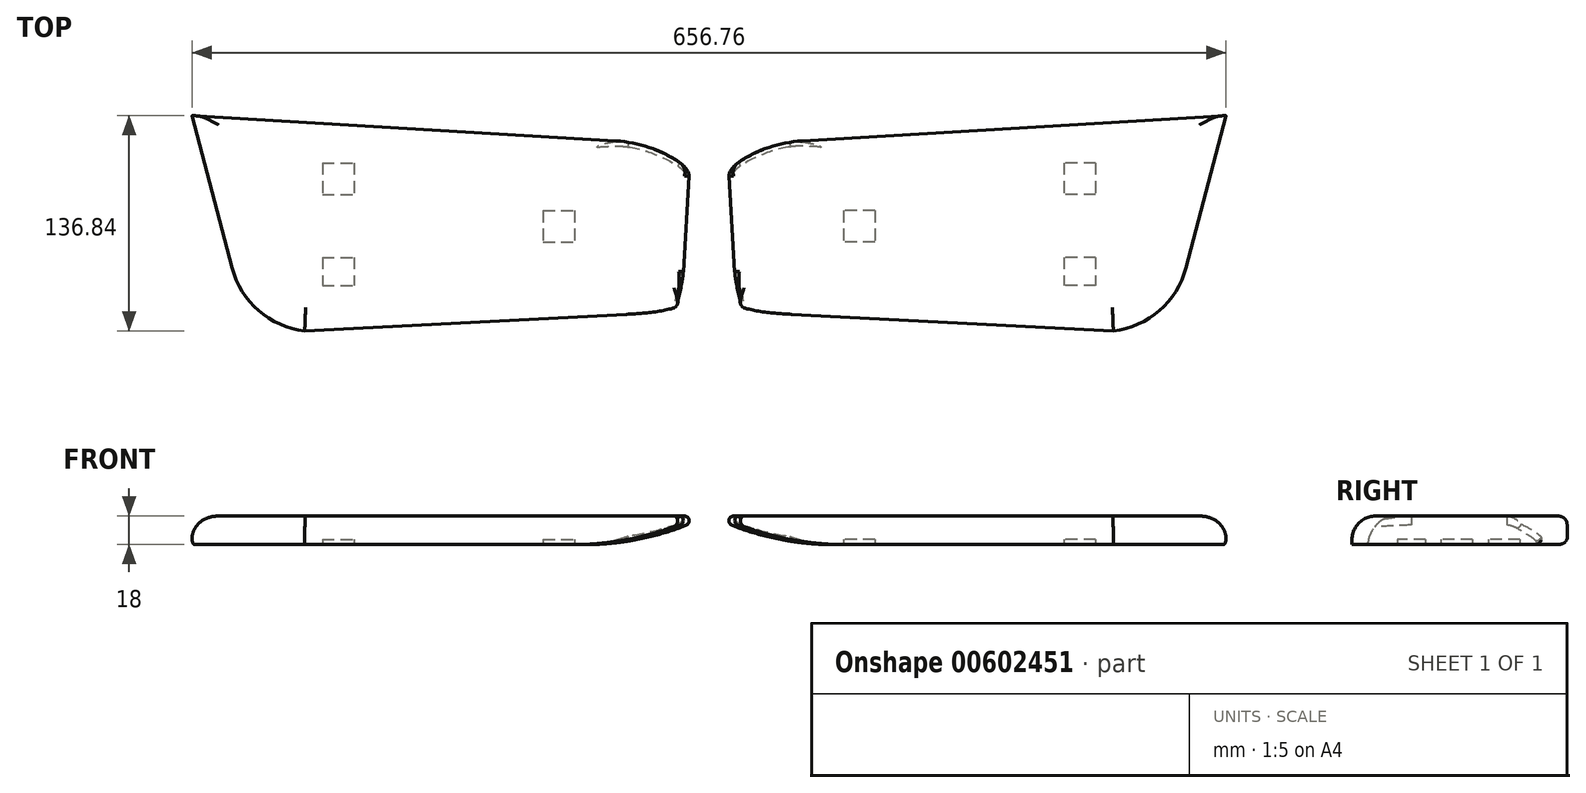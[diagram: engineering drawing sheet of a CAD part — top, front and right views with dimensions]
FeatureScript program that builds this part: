
annotation { "Feature Type Name" : "Feature", "Feature Type Description" : "" }
export const myFeature = defineFeature(function(context is Context, id is Id, definition is map)
    precondition{}
    {
        {
            var Q0;
            Q0=qCreatedBy(makeId("Top.planeOp"),FACE);
            var sketch = newSketch(context, id + "F0", { "sketchPlane" : qUnion([Q0])});
            skPoint(sketch, "E0.endSnap0", {"position": v(0, 40) * mm});
            skLineSegment(sketch, "E1", {"start": v(78.9, 93.27) * mm, "end": v(328.44, 108.2) * mm});
            skPoint(sketch, "E2.visualSharp", {"position": v(0, 0) * mm});
            skPoint(sketch, "E3.visualSharp", {"position": v(0, 80) * mm});
            skLineSegment(sketch, "E4", {"start": v(78.9, 93.27) * mm, "end": v(58.93, 92.08) * mm});
            skArc(sketch, "E5", {"start": v(58.93, 92.08) * mm, "mid": v(26.05, 82.83) * mm, "end": v(0, 60.74) * mm});
            skLineSegment(sketch, "E6", {"start": v(328.44, 108.2) * mm, "end": v(302.97, 11.5) * mm});
            skLineSegment(sketch, "E7", {"start": v(0, 60.74) * mm, "end": v(21.15, -16.42) * mm});
            skLineSegment(sketch, "E8", {"start": v(21.15, -16.42) * mm, "end": v(256.77, -28.64) * mm});
            skArc(sketch, "E9", {"start": v(256.77, -28.64) * mm, "mid": v(286.06, -15.68) * mm, "end": v(302.97, 11.5) * mm});
            skSolve(sketch);
        }
        {
            var Q0;
            {var subQ4=sQuery(id+"F0.wireOp",EDGE,"E1");Q0=makeQuery(id+"F0.imprint","IMPRINT",FACE,{"disambiguationData":[TD([[makeQuery(id+"F0.imprint","IMPRINT",EDGE,{"derivedFrom":subQ4}),-1.0]])]});}
            var Q1;
            Q1=makeQuery(id+"F0.imprint","IMPRINT",FACE,{"disambiguationData":[TD([[makeQuery(id+"F0.imprint","IMPRINT",EDGE,{"derivedFrom":sQuery(id+"F0.wireOp",EDGE,"sUsfVo84-EZPH-Wl4j-0lNI-KG4tjsNKiTaD")}),1.0]])]});
            extrude(context, id + "F1", {"entities" : qUnion([Q0, Q1]), "depth" : 18 * mm, "offsetDistance" : 25 * mm});
        }
        {
            var Q0;
            Q0=makeQuery(id+"F1.opExtrude","SWEPT_FACE",FACE,{"disambiguationData":[OSD([sQuery(id+"F0.wireOp",EDGE,"E5")])]});
            var Q1;
            Q1=makeQuery(id+"F1.opExtrude","SWEPT_FACE",FACE,{"disambiguationData":[OSD([sQuery(id+"F0.wireOp",EDGE,"E7")])]});
            fillet(context, id + "F2", {"entities" : qUnion([Q0, Q1]), "radius" : 5 * mm, "tangentPropagation" : true, "allowEdgeOverflow" : false});
        }
        {
            var Q0;
            Q0=makeQuery(id+"F1.opExtrude","CAP_EDGE",EDGE,{"disambiguationData":[OSD([sQuery(id+"F0.wireOp",EDGE,"E8")])],"isStart":false});
            var Q1;
            Q1=makeQuery(id+"F1.opExtrude","CAP_EDGE",EDGE,{"disambiguationData":[OSD([sQuery(id+"F0.wireOp",EDGE,"E9")])],"isStart":false});
            var Q2;
            Q2=makeQuery(id+"F1.opExtrude","CAP_EDGE",EDGE,{"disambiguationData":[OSD([sQuery(id+"F0.wireOp",EDGE,"E6")])],"isStart":false});
            fillet(context, id + "F3", {"entities" : qUnion([Q0, Q1, Q2]), "radius" : 15 * mm, "allowEdgeOverflow" : false});
        }
        {
            var Q0;
            Q0=makeQuery(id+"F1.opExtrude","SWEPT_BODY",BODY,{"disambiguationData":[OSD([sQuery(id+"F0.wireOp",EDGE,"E1"),sQuery(id+"F0.wireOp",EDGE,"E4"),sQuery(id+"F0.wireOp",EDGE,"E5"),sQuery(id+"F0.wireOp",EDGE,"E6"),sQuery(id+"F0.wireOp",EDGE,"E7"),sQuery(id+"F0.wireOp",EDGE,"E8"),sQuery(id+"F0.wireOp",EDGE,"E9")])]});
            var Q1;
            Q1=qCreatedBy(makeId("Right.planeOp"),FACE);
            mirror(context, id + "F4", {"entities" : qUnion([Q0]), "mirrorPlane" : qUnion([Q1])});
        }
        {
            var Q0;
            Q0=makeQuery(id+"F4.opPattern","COPY",FACE,{"derivedFrom":makeQuery(id+"F1.opExtrude","SWEPT_FACE",FACE,{"disambiguationData":[OSD([sQuery(id+"F0.wireOp",EDGE,"E1"),sQuery(id+"F0.wireOp",EDGE,"E4")])]}),"instanceName":"1"});
            var sketch = newSketch(context, id + "F5", { "sketchPlane" : qUnion([Q0])});
            skArc(sketch, "E10", {"start": v(-6.1, 23.9) * mm, "mid": v(33.74, 7.16) * mm, "end": v(76.36, 0) * mm});
            skLineSegment(sketch, "E11", {"start": v(-6.1, 23.9) * mm, "end": v(-6.1, 0) * mm});
            skLineSegment(sketch, "E12", {"start": v(-6.1, 0) * mm, "end": v(76.36, 0) * mm});
            skSolve(sketch);
        }
        {
            var Q0;
            Q0=makeQuery(id+"F5.imprint","IMPRINT",FACE,{"disambiguationData":[TD([[makeQuery(id+"F5.imprint","IMPRINT",EDGE,{"derivedFrom":sQuery(id+"F5.wireOp",EDGE,"E10")}),-1.0]])]});
            var Q1;
            Q1=makeQuery(id+"F4.opPattern","COPY",FACE,{"derivedFrom":makeQuery(id+"F1.opExtrude","SWEPT_FACE",FACE,{"disambiguationData":[OSD([sQuery(id+"F0.wireOp",EDGE,"E8")])]}),"instanceName":"1"});
            extrude(context, id + "F6", {"entities" : qUnion([Q0]), "operationType" : NewBodyOperationType.REMOVE, "endBound" : BoundingType.UP_TO_SURFACE, "oppositeDirection" : true, "depth" : 200 * mm, "endBoundEntityFace" : qUnion([Q1]), "offsetDistance" : 25 * mm});
        }
        {
            var Q0;
            {var subQ0=sQuery(id+"F0.wireOp",EDGE,"E7");Q0=makeQuery(id+"F6.boolean.opBoolean","INTERSECT",EDGE,{"derivedFrom":[makeQuery(id+"F4.opPattern","COPY",FACE,{"derivedFrom":makeQuery(id+"F2.opFillet","BLEND_FACE",FACE,{"disambiguationData":[OSD([subQ0]),TDD([makeQuery(id+"F1.opExtrude","CAP_EDGE",EDGE,{"disambiguationData":[OSD([subQ0])],"isStart":false})])]}),"instanceName":"1"}),makeQuery(id+"F6.opExtrude","SWEPT_FACE",FACE,{"disambiguationData":[OSD([sQuery(id+"F5.wireOp",EDGE,"E10")])]})]});}
            var Q1;
            Q1=makeQuery(id+"F6.boolean.opBoolean","INTERSECT",EDGE,{"derivedFrom":[makeQuery(id+"F4.opPattern","COPY",FACE,{"derivedFrom":makeQuery(id+"F1.opExtrude","SWEPT_FACE",FACE,{"disambiguationData":[OSD([sQuery(id+"F0.wireOp",EDGE,"E7")])]}),"instanceName":"1"}),makeQuery(id+"F6.opExtrude","SWEPT_FACE",FACE,{"disambiguationData":[OSD([sQuery(id+"F5.wireOp",EDGE,"E10")])]})]});
            fillet(context, id + "F7", {"entities" : qUnion([Q0, Q1]), "radius" : 3 * mm, "tangentPropagation" : true, "allowEdgeOverflow" : false});
        }
        {
            var Q0;
            Q0=makeQuery(id+"F1.opExtrude","CAP_FACE",FACE,{"disambiguationData":[OSD([sQuery(id+"F0.wireOp",EDGE,"E1"),sQuery(id+"F0.wireOp",EDGE,"E4"),sQuery(id+"F0.wireOp",EDGE,"E5"),sQuery(id+"F0.wireOp",EDGE,"E6"),sQuery(id+"F0.wireOp",EDGE,"E7"),sQuery(id+"F0.wireOp",EDGE,"E8"),sQuery(id+"F0.wireOp",EDGE,"E9")])],"isStart":true});
            var sketch = newSketch(context, id + "F8", { "sketchPlane" : qUnion([Q0])});
            skLineSegment(sketch, "E13.bottom", {"start": v(245.51, -78.1) * mm, "end": v(225.51, -78.1) * mm});
            skLineSegment(sketch, "E13.top", {"start": v(245.51, -58.1) * mm, "end": v(225.51, -58.1) * mm});
            skLineSegment(sketch, "E13.left", {"start": v(245.51, -78.1) * mm, "end": v(245.51, -58.1) * mm});
            skLineSegment(sketch, "E13.right", {"start": v(225.51, -78.1) * mm, "end": v(225.51, -58.1) * mm});
            skLineSegment(sketch, "E14.bottom", {"start": v(245.51, -18.1) * mm, "end": v(225.51, -18.1) * mm});
            skLineSegment(sketch, "E14.top", {"start": v(245.51, -0.17) * mm, "end": v(225.51, -0.17) * mm});
            skLineSegment(sketch, "E14.left", {"start": v(245.51, -18.1) * mm, "end": v(245.51, -0.17) * mm});
            skLineSegment(sketch, "E14.right", {"start": v(225.51, -18.1) * mm, "end": v(225.51, -0.17) * mm});
            skLineSegment(sketch, "E15.bottom", {"start": v(105.37, -47.91) * mm, "end": v(85.37, -47.91) * mm});
            skLineSegment(sketch, "E15.top", {"start": v(105.37, -27.91) * mm, "end": v(85.37, -27.91) * mm});
            skLineSegment(sketch, "E15.left", {"start": v(105.37, -47.91) * mm, "end": v(105.37, -27.91) * mm});
            skLineSegment(sketch, "E15.right", {"start": v(85.37, -47.91) * mm, "end": v(85.37, -27.91) * mm});
            skLineSegment(sketch, "E16", {"start": v(225.51, -58.1) * mm, "end": v(225.51, -18.1) * mm});
            skLineSegment(sketch, "E17", {"start": v(225.51, -38.1) * mm, "end": v(105.37, -38.1) * mm});
            skLineSegment(sketch, "E18.MirrorCS", {"start": v(-105.37, -47.91) * mm, "end": v(-105.37, -27.91) * mm});
            skLineSegment(sketch, "E19.MirrorCS", {"start": v(-105.37, -47.91) * mm, "end": v(-85.37, -47.91) * mm});
            skLineSegment(sketch, "E20.MirrorCS", {"start": v(-245.51, -78.1) * mm, "end": v(-225.51, -78.1) * mm});
            skLineSegment(sketch, "E21.MirrorCS", {"start": v(-85.37, -47.91) * mm, "end": v(-85.37, -27.91) * mm});
            skLineSegment(sketch, "E22.MirrorCS", {"start": v(-225.51, -58.1) * mm, "end": v(-225.51, -18.1) * mm});
            skLineSegment(sketch, "E23.MirrorCS", {"start": v(-225.51, -78.1) * mm, "end": v(-225.51, -58.1) * mm});
            skLineSegment(sketch, "E24.MirrorCS", {"start": v(-225.51, -18.1) * mm, "end": v(-225.51, -0.17) * mm});
            skLineSegment(sketch, "E25.MirrorCS", {"start": v(-245.51, -0.17) * mm, "end": v(-225.51, -0.17) * mm});
            skLineSegment(sketch, "E26.MirrorCS", {"start": v(-105.37, -27.91) * mm, "end": v(-85.37, -27.91) * mm});
            skLineSegment(sketch, "E27.MirrorCS", {"start": v(-225.51, -38.1) * mm, "end": v(-105.37, -38.1) * mm});
            skLineSegment(sketch, "E28.MirrorCS", {"start": v(-245.51, -18.1) * mm, "end": v(-225.51, -18.1) * mm});
            skLineSegment(sketch, "E29.MirrorCS", {"start": v(-245.51, -58.1) * mm, "end": v(-225.51, -58.1) * mm});
            skLineSegment(sketch, "E30.MirrorCS", {"start": v(-245.51, -78.1) * mm, "end": v(-245.51, -58.1) * mm});
            skLineSegment(sketch, "E31.MirrorCS", {"start": v(-245.51, -18.1) * mm, "end": v(-245.51, -0.17) * mm});
            skSolve(sketch);
        }
        {
            var Q0;
            Q0=makeQuery(id+"F1.opExtrude","SWEPT_BODY",BODY,{"disambiguationData":[OSD([sQuery(id+"F0.wireOp",EDGE,"E1"),sQuery(id+"F0.wireOp",EDGE,"E4"),sQuery(id+"F0.wireOp",EDGE,"E5"),sQuery(id+"F0.wireOp",EDGE,"E6"),sQuery(id+"F0.wireOp",EDGE,"E7"),sQuery(id+"F0.wireOp",EDGE,"E8"),sQuery(id+"F0.wireOp",EDGE,"E9")])]});
            deleteBodies(context, id + "F9", {"entities" : qUnion([Q0])});
        }
        {
            var Q0;
            Q0=makeQuery(id+"F4.opPattern","COPY",BODY,{"derivedFrom":makeQuery(id+"F1.opExtrude","SWEPT_BODY",BODY,{"disambiguationData":[OSD([sQuery(id+"F0.wireOp",EDGE,"E1"),sQuery(id+"F0.wireOp",EDGE,"E4"),sQuery(id+"F0.wireOp",EDGE,"E5"),sQuery(id+"F0.wireOp",EDGE,"E6"),sQuery(id+"F0.wireOp",EDGE,"E7"),sQuery(id+"F0.wireOp",EDGE,"E8"),sQuery(id+"F0.wireOp",EDGE,"E9")])]}),"instanceName":"1"});
            var Q1;
            Q1=qCreatedBy(makeId("Right.planeOp"),FACE);
            mirror(context, id + "F10", {"entities" : qUnion([Q0]), "mirrorPlane" : qUnion([Q1])});
        }
        {
            var Q0;
            Q0=makeQuery(id+"F8.imprint","IMPRINT",FACE,{"disambiguationData":[TD([[makeQuery(id+"F8.imprint","IMPRINT",EDGE,{"derivedFrom":sQuery(id+"F8.wireOp",EDGE,"E24.MirrorCS")}),1.0]])]});
            var Q1;
            Q1=makeQuery(id+"F8.imprint","IMPRINT",FACE,{"disambiguationData":[TD([[makeQuery(id+"F8.imprint","IMPRINT",EDGE,{"derivedFrom":sQuery(id+"F8.wireOp",EDGE,"E20.MirrorCS")}),1.0]])]});
            var Q2;
            {var subQ0=sQuery(id+"F8.wireOp",EDGE,"E19.MirrorCS");Q2=makeQuery(id+"F8.imprint","IMPRINT",FACE,{"disambiguationData":[TD([[makeQuery(id+"F8.imprint","IMPRINT",EDGE,{"derivedFrom":subQ0}),1.0]])]});}
            var Q3;
            {var subQ3=sQuery(id+"F8.wireOp",EDGE,"E15.bottom");Q3=makeQuery(id+"F8.imprint","IMPRINT",FACE,{"disambiguationData":[TD([[makeQuery(id+"F8.imprint","IMPRINT",EDGE,{"derivedFrom":subQ3}),-1.0]])]});}
            var Q4;
            Q4=makeQuery(id+"F8.imprint","IMPRINT",FACE,{"disambiguationData":[TD([[makeQuery(id+"F8.imprint","IMPRINT",EDGE,{"derivedFrom":sQuery(id+"F8.wireOp",EDGE,"E14.bottom")}),-1.0]])]});
            var Q5;
            Q5=makeQuery(id+"F8.imprint","IMPRINT",FACE,{"disambiguationData":[TD([[makeQuery(id+"F8.imprint","IMPRINT",EDGE,{"derivedFrom":sQuery(id+"F8.wireOp",EDGE,"E13.bottom")}),-1.0]])]});
            extrude(context, id + "F11", {"entities" : qUnion([Q0, Q1, Q2, Q3, Q4, Q5]), "operationType" : NewBodyOperationType.REMOVE, "oppositeDirection" : true, "depth" : 3 * mm, "offsetDistance" : 25 * mm});
        }
    });
